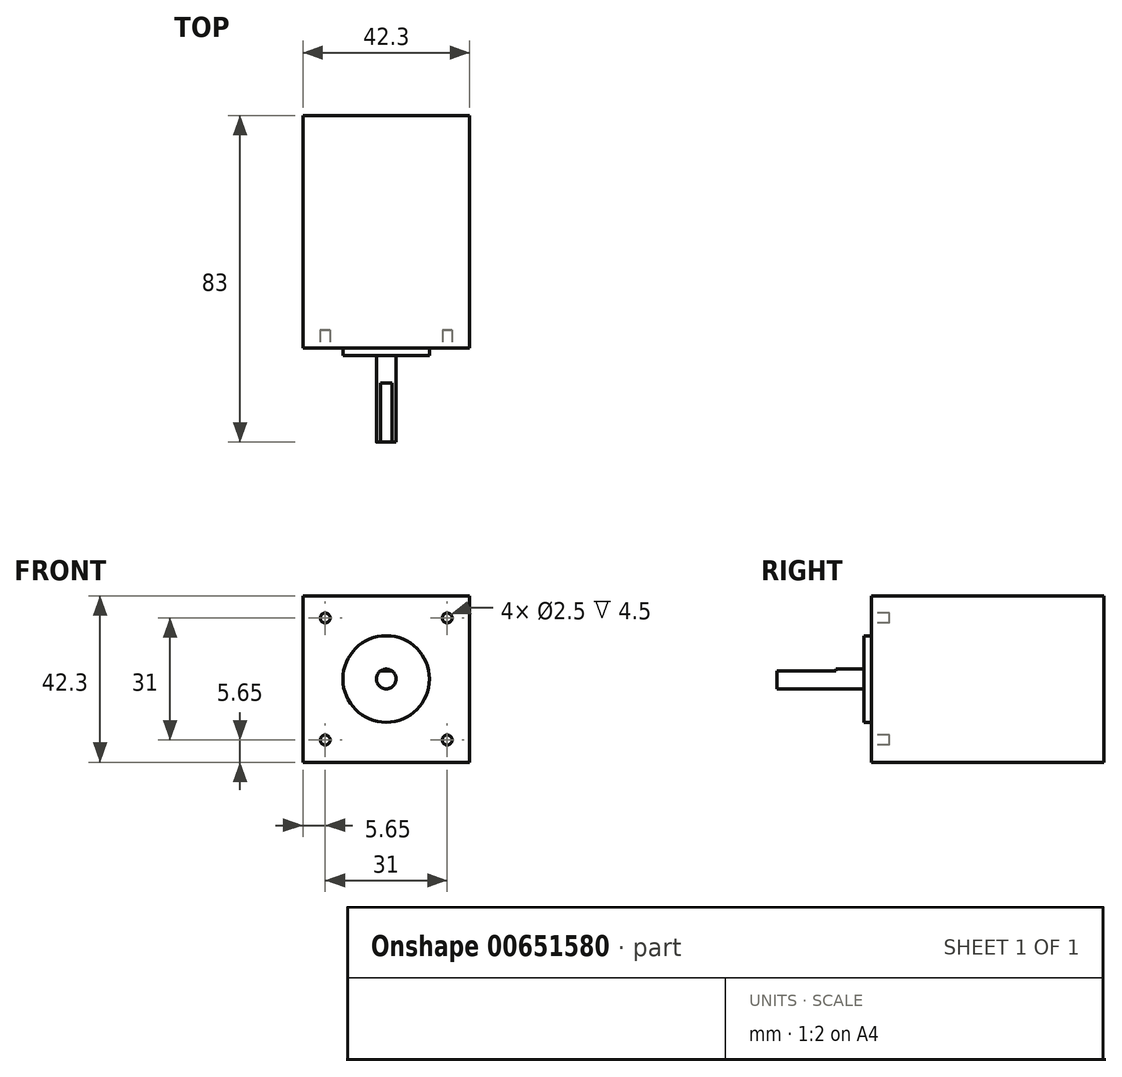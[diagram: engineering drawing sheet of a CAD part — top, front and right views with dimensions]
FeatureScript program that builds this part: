
annotation { "Feature Type Name" : "Feature", "Feature Type Description" : "" }
export const myFeature = defineFeature(function(context is Context, id is Id, definition is map)
    precondition{}
    {
        {
            var Q0;
            Q0=qCreatedBy(makeId("Front.planeOp"),FACE);
            var sketch = newSketch(context, id + "F0", { "sketchPlane" : qUnion([Q0])});
            skLineSegment(sketch, "E0.bottom", {"start": v(-21.15, 21.15) * mm, "end": v(21.15, 21.15) * mm});
            skLineSegment(sketch, "E0.top", {"start": v(-21.15, -21.15) * mm, "end": v(21.15, -21.15) * mm});
            skLineSegment(sketch, "E0.left", {"start": v(-21.15, 21.15) * mm, "end": v(-21.15, -21.15) * mm});
            skLineSegment(sketch, "E0.right", {"start": v(21.15, 21.15) * mm, "end": v(21.15, -21.15) * mm});
            skPoint(sketch, "E1", {"position": v(0, 0) * mm});
            skSolve(sketch);
        }
        {
            var Q0;
            Q0=makeQuery(id+"F0.imprint","IMPRINT",FACE,{"disambiguationData":[TD([[makeQuery(id+"F0.imprint","IMPRINT",EDGE,{"derivedFrom":sQuery(id+"F0.wireOp",EDGE,"E0.bottom")}),-1.0]])]});
            extrude(context, id + "F1", {"entities" : qUnion([Q0]), "depth" : 59 * mm});
        }
        {
            var Q0;
            Q0=makeQuery(id+"F1.opExtrude","CAP_FACE",FACE,{"disambiguationData":[OSD([sQuery(id+"F0.wireOp",EDGE,"E0.bottom"),sQuery(id+"F0.wireOp",EDGE,"E0.top"),sQuery(id+"F0.wireOp",EDGE,"E0.left"),sQuery(id+"F0.wireOp",EDGE,"E0.right")])],"isStart":false});
            var sketch = newSketch(context, id + "F2", { "sketchPlane" : qUnion([Q0])});
            skCircle(sketch, "E2", {"center": v(0, 0) * mm, "radius": 11 * mm});
            skSolve(sketch);
        }
        {
            var Q0;
            Q0=makeQuery(id+"F2.imprint","IMPRINT",FACE,{"disambiguationData":[TD([[makeQuery(id+"F2.imprint","IMPRINT",EDGE,{"derivedFrom":sQuery(id+"F2.wireOp",EDGE,"E2")}),1.0]])]});
            extrude(context, id + "F3", {"entities" : qUnion([Q0]), "operationType" : NewBodyOperationType.ADD, "depth" : 2 * mm});
        }
        {
            var Q0;
            Q0=makeQuery(id+"F3.opExtrude","CAP_FACE",FACE,{"disambiguationData":[OSD([sQuery(id+"F2.wireOp",EDGE,"E2")])],"isStart":false});
            var sketch = newSketch(context, id + "F4", { "sketchPlane" : qUnion([Q0])});
            skCircle(sketch, "E3", {"center": v(0, 0) * mm, "radius": 2.5 * mm});
            skSolve(sketch);
        }
        {
            var Q0;
            Q0=makeQuery(id+"F4.imprint","IMPRINT",FACE,{"disambiguationData":[TD([[makeQuery(id+"F4.imprint","IMPRINT",EDGE,{"derivedFrom":sQuery(id+"F4.wireOp",EDGE,"E3")}),1.0]])]});
            extrude(context, id + "F5", {"entities" : qUnion([Q0]), "operationType" : NewBodyOperationType.ADD, "depth" : 22 * mm});
        }
        {
            var Q0;
            Q0=makeQuery(id+"F5.opExtrude","CAP_FACE",FACE,{"disambiguationData":[OSD([sQuery(id+"F4.wireOp",EDGE,"E3")])],"isStart":false});
            var sketch = newSketch(context, id + "F6", { "sketchPlane" : qUnion([Q0])});
            skLineSegment(sketch, "E4", {"start": v(-1.5, 2) * mm, "end": v(1.5, 2) * mm});
            skLineSegment(sketch, "E5", {"start": v(0, 2.5) * mm, "end": v(0, 2) * mm});
            skSolve(sketch);
        }
        {
            var Q0;
            {var subQ3=sQuery(id+"F6.wireOp",EDGE,"E5");Q0=makeQuery(id+"F6.imprint","IMPRINT",FACE,{"disambiguationData":[TD([[makeQuery(id+"F6.imprint","IMPRINT",EDGE,{"derivedFrom":subQ3}),-1.0]])]});}
            var Q1;
            {var subQ3=sQuery(id+"F6.wireOp",EDGE,"E5");Q1=makeQuery(id+"F6.imprint","IMPRINT",FACE,{"disambiguationData":[TD([[makeQuery(id+"F6.imprint","IMPRINT",EDGE,{"derivedFrom":subQ3}),1.0]])]});}
            extrude(context, id + "F7", {"entities" : qUnion([Q0, Q1]), "operationType" : NewBodyOperationType.REMOVE, "oppositeDirection" : true, "depth" : 15 * mm});
        }
        {
            var Q0;
            Q0=makeQuery(id+"F1.opExtrude","CAP_FACE",FACE,{"disambiguationData":[OSD([sQuery(id+"F0.wireOp",EDGE,"E0.bottom"),sQuery(id+"F0.wireOp",EDGE,"E0.top"),sQuery(id+"F0.wireOp",EDGE,"E0.left"),sQuery(id+"F0.wireOp",EDGE,"E0.right")])],"isStart":false});
            var sketch = newSketch(context, id + "F8", { "sketchPlane" : qUnion([Q0])});
            skLineSegment(sketch, "E6.bottom", {"start": v(-15.5, 15.5) * mm, "end": v(15.5, 15.5) * mm});
            skLineSegment(sketch, "E6.top", {"start": v(-15.5, -15.5) * mm, "end": v(15.5, -15.5) * mm});
            skLineSegment(sketch, "E6.left", {"start": v(-15.5, 15.5) * mm, "end": v(-15.5, -15.5) * mm});
            skLineSegment(sketch, "E6.right", {"start": v(15.5, 15.5) * mm, "end": v(15.5, -15.5) * mm});
            skPoint(sketch, "E7", {"position": v(0, 0) * mm});
            skCircle(sketch, "E8", {"center": v(-15.5, 15.5) * mm, "radius": 1.25 * mm});
            skCircle(sketch, "E9", {"center": v(15.5, 15.5) * mm, "radius": 1.25 * mm});
            skCircle(sketch, "E10", {"center": v(-15.5, -15.5) * mm, "radius": 1.25 * mm});
            skCircle(sketch, "E11", {"center": v(15.5, -15.5) * mm, "radius": 1.25 * mm});
            skSolve(sketch);
        }
        {
            var Q0;
            {var subQ0=sQuery(id+"F8.wireOp",EDGE,"E6.right");var subQ1=sQuery(id+"F8.wireOp",EDGE,"E6.bottom");var subQ2=makeQuery(id+"F8.imprint","INTERSECT",VERTEX,{"derivedFrom":[subQ1,subQ0]});Q0=makeQuery(id+"F8.imprint","IMPRINT",FACE,{"disambiguationData":[TD([[makeQuery(id+"F8.imprint","IMPRINT",EDGE,{"disambiguationData":[TD([[subQ2,1.0]])],"derivedFrom":subQ1}),1.0]])]});}
            var Q1;
            {var subQ0=sQuery(id+"F8.wireOp",EDGE,"E6.right");var subQ1=sQuery(id+"F8.wireOp",EDGE,"E6.bottom");var subQ2=makeQuery(id+"F8.imprint","INTERSECT",VERTEX,{"derivedFrom":[subQ1,subQ0]});Q1=makeQuery(id+"F8.imprint","IMPRINT",FACE,{"disambiguationData":[TD([[makeQuery(id+"F8.imprint","IMPRINT",EDGE,{"disambiguationData":[TD([[subQ2,1.0]])],"derivedFrom":subQ1}),-1.0]])]});}
            var Q2;
            {var subQ0=sQuery(id+"F8.wireOp",EDGE,"E6.left");var subQ1=sQuery(id+"F8.wireOp",EDGE,"E6.bottom");var subQ2=makeQuery(id+"F8.imprint","INTERSECT",VERTEX,{"derivedFrom":[subQ1,subQ0]});Q2=makeQuery(id+"F8.imprint","IMPRINT",FACE,{"disambiguationData":[TD([[makeQuery(id+"F8.imprint","IMPRINT",EDGE,{"disambiguationData":[TD([[subQ2,-1.0]])],"derivedFrom":subQ1}),1.0]])]});}
            var Q3;
            {var subQ0=sQuery(id+"F8.wireOp",EDGE,"E6.left");var subQ1=sQuery(id+"F8.wireOp",EDGE,"E6.bottom");var subQ2=makeQuery(id+"F8.imprint","INTERSECT",VERTEX,{"derivedFrom":[subQ1,subQ0]});Q3=makeQuery(id+"F8.imprint","IMPRINT",FACE,{"disambiguationData":[TD([[makeQuery(id+"F8.imprint","IMPRINT",EDGE,{"disambiguationData":[TD([[subQ2,-1.0]])],"derivedFrom":subQ1}),-1.0]])]});}
            var Q4;
            {var subQ0=sQuery(id+"F8.wireOp",EDGE,"E6.left");var subQ1=sQuery(id+"F8.wireOp",EDGE,"E6.top");var subQ2=makeQuery(id+"F8.imprint","INTERSECT",VERTEX,{"derivedFrom":[subQ1,subQ0]});Q4=makeQuery(id+"F8.imprint","IMPRINT",FACE,{"disambiguationData":[TD([[makeQuery(id+"F8.imprint","IMPRINT",EDGE,{"disambiguationData":[TD([[subQ2,-1.0]])],"derivedFrom":subQ1}),-1.0]])]});}
            var Q5;
            {var subQ0=sQuery(id+"F8.wireOp",EDGE,"E6.left");var subQ1=sQuery(id+"F8.wireOp",EDGE,"E6.top");var subQ2=makeQuery(id+"F8.imprint","INTERSECT",VERTEX,{"derivedFrom":[subQ1,subQ0]});Q5=makeQuery(id+"F8.imprint","IMPRINT",FACE,{"disambiguationData":[TD([[makeQuery(id+"F8.imprint","IMPRINT",EDGE,{"disambiguationData":[TD([[subQ2,-1.0]])],"derivedFrom":subQ1}),1.0]])]});}
            var Q6;
            {var subQ0=sQuery(id+"F8.wireOp",EDGE,"E6.right");var subQ1=sQuery(id+"F8.wireOp",EDGE,"E6.top");var subQ2=makeQuery(id+"F8.imprint","INTERSECT",VERTEX,{"derivedFrom":[subQ1,subQ0]});Q6=makeQuery(id+"F8.imprint","IMPRINT",FACE,{"disambiguationData":[TD([[makeQuery(id+"F8.imprint","IMPRINT",EDGE,{"disambiguationData":[TD([[subQ2,1.0]])],"derivedFrom":subQ1}),1.0]])]});}
            var Q7;
            {var subQ0=sQuery(id+"F8.wireOp",EDGE,"E6.right");var subQ1=sQuery(id+"F8.wireOp",EDGE,"E6.top");var subQ2=makeQuery(id+"F8.imprint","INTERSECT",VERTEX,{"derivedFrom":[subQ1,subQ0]});Q7=makeQuery(id+"F8.imprint","IMPRINT",FACE,{"disambiguationData":[TD([[makeQuery(id+"F8.imprint","IMPRINT",EDGE,{"disambiguationData":[TD([[subQ2,1.0]])],"derivedFrom":subQ1}),-1.0]])]});}
            extrude(context, id + "F9", {"entities" : qUnion([Q0, Q1, Q2, Q3, Q4, Q5, Q6, Q7]), "operationType" : NewBodyOperationType.REMOVE, "oppositeDirection" : true, "depth" : 4.5 * mm});
        }
    });
